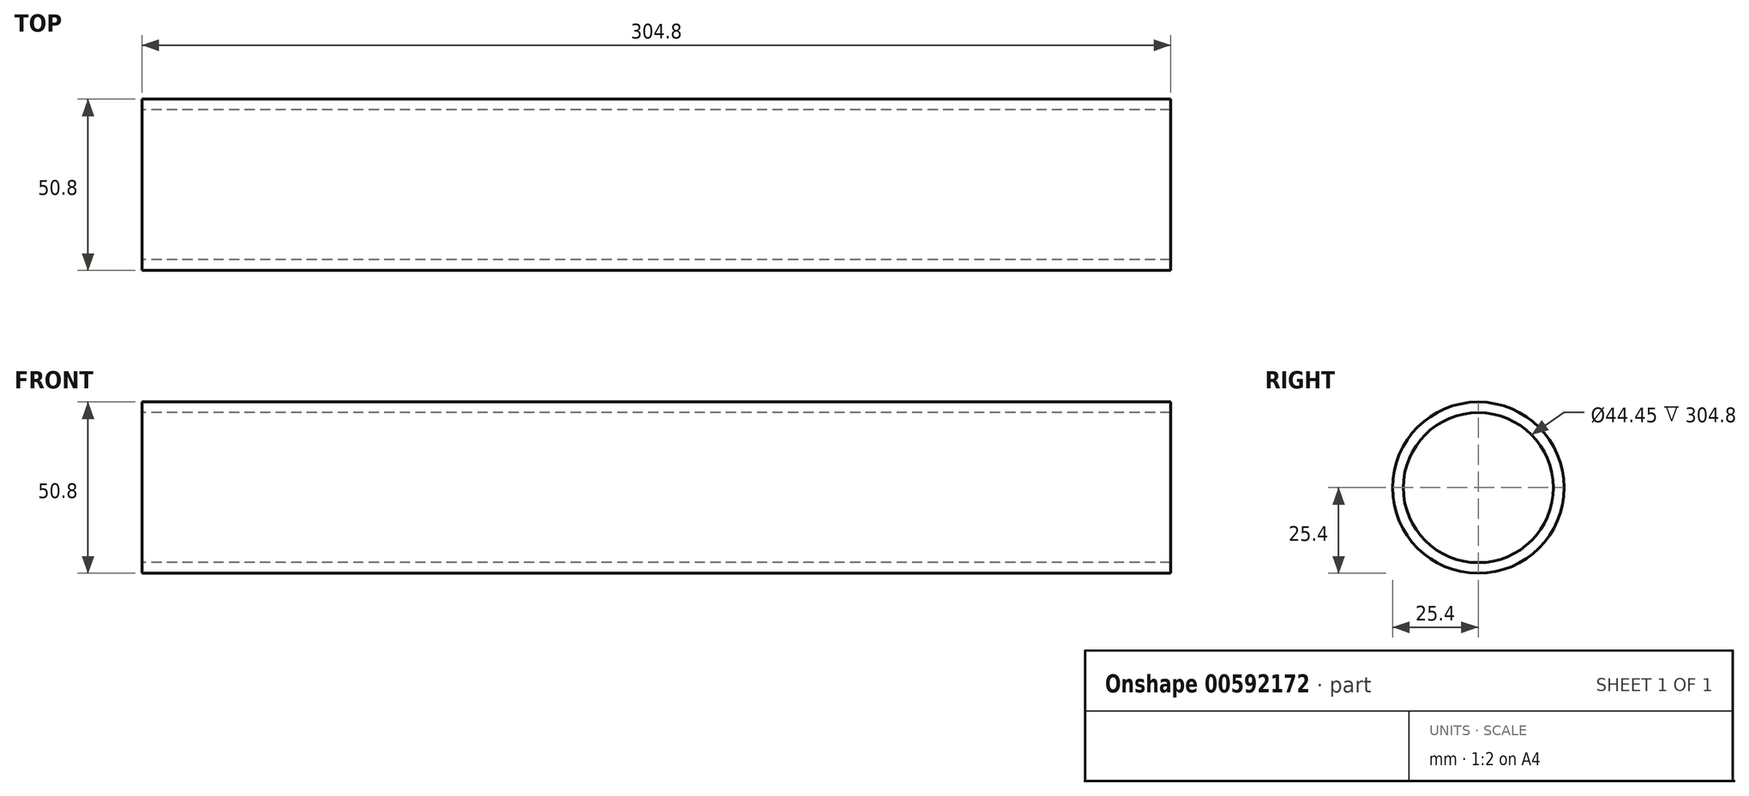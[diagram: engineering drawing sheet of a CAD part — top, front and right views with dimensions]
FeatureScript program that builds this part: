
annotation { "Feature Type Name" : "Feature", "Feature Type Description" : "" }
export const myFeature = defineFeature(function(context is Context, id is Id, definition is map)
    precondition{}
    {
        {
            var Q0;
            Q0=qCreatedBy(makeId("Right.planeOp"),FACE);
            var sketch = newSketch(context, id + "F0", { "sketchPlane" : qUnion([Q0])});
            skCircle(sketch, "E0", {"center": v(0, 0) * mm, "radius": 25.4 * mm});
            skCircle(sketch, "E1.0", {"center": v(0, 0) * mm, "radius": 22.23 * mm});
            skSolve(sketch);
        }
        {
            var Q0;
            Q0 = qSketchRegion(id + "F0", true);
            extrude(context, id + "F1", {"entities" : qUnion([Q0]), "depth" : 304.8 * mm, "offsetDistance" : 25.4 * mm});
        }
    });
